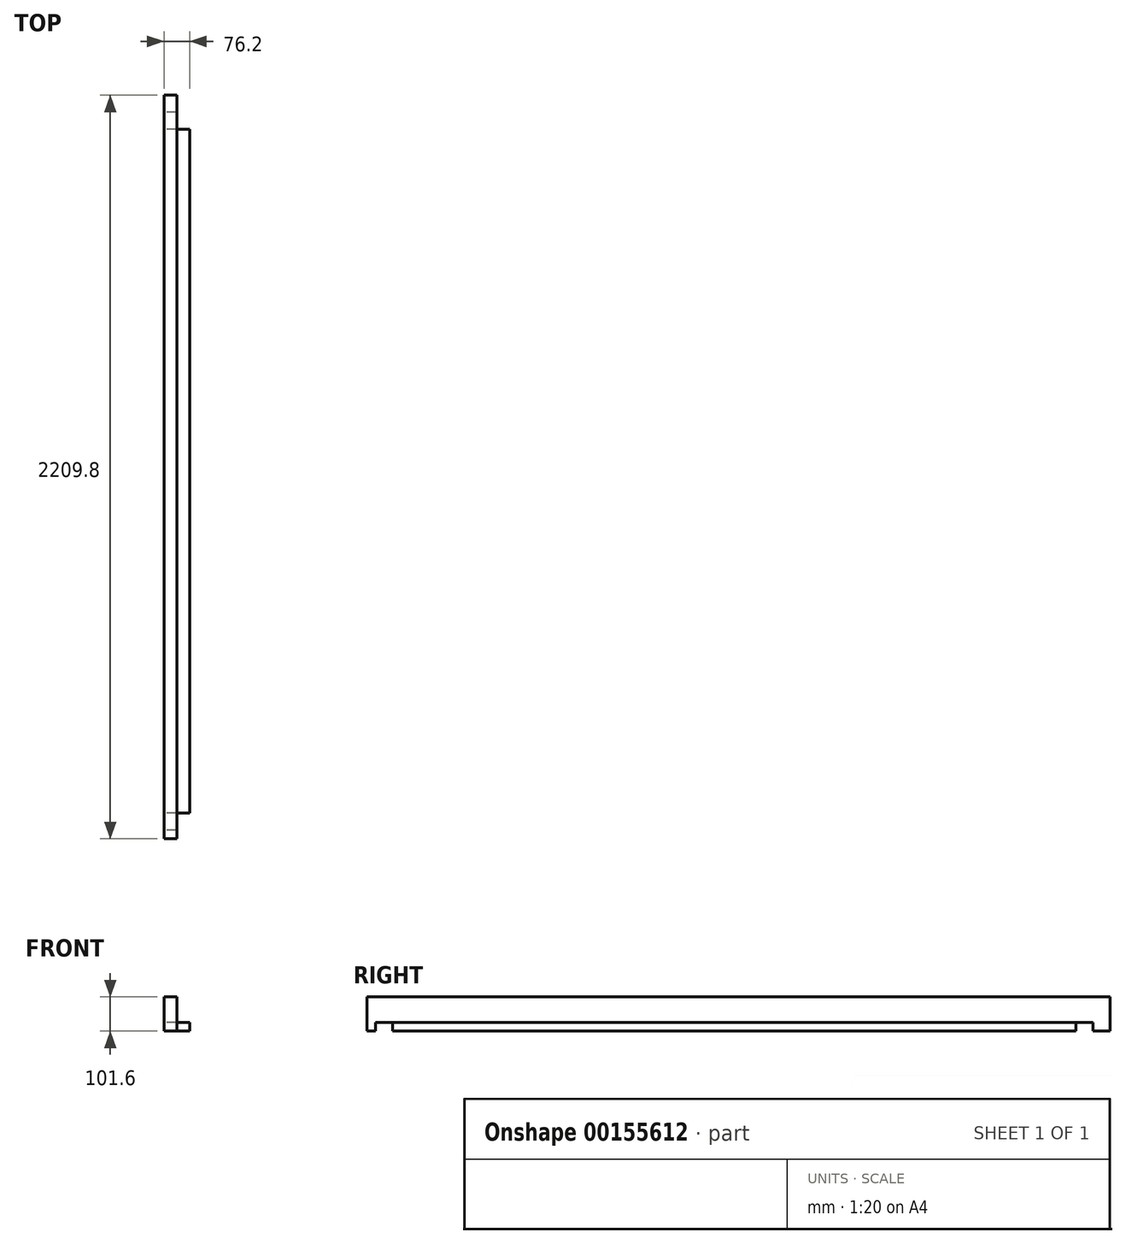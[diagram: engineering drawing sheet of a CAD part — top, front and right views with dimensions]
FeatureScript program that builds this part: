
annotation { "Feature Type Name" : "Feature", "Feature Type Description" : "" }
export const myFeature = defineFeature(function(context is Context, id is Id, definition is map)
    precondition{}
    {
        {
            var Q0;
            Q0=qCreatedBy(makeId("Right.planeOp"),FACE);
            var sketch = newSketch(context, id + "F0", { "sketchPlane" : qUnion([Q0])});
            skLineSegment(sketch, "E0.bottom", {"start": v(-1104.9, 50.8) * mm, "end": v(1104.9, 50.8) * mm});
            skLineSegment(sketch, "E0.top", {"start": v(-1104.9, -50.8) * mm, "end": v(1104.9, -50.8) * mm});
            skLineSegment(sketch, "E0.left", {"start": v(-1104.9, 50.8) * mm, "end": v(-1104.9, -50.8) * mm});
            skLineSegment(sketch, "E0.right", {"start": v(1104.9, 50.8) * mm, "end": v(1104.9, -50.8) * mm});
            skPoint(sketch, "E0.middle", {"position": v(0, 0) * mm});
            skLineSegment(sketch, "E1.bottom", {"start": v(1054.1, -50.8) * mm, "end": v(1003.3, -50.8) * mm});
            skLineSegment(sketch, "E1.top", {"start": v(1054.1, -25.4) * mm, "end": v(1003.3, -25.4) * mm});
            skLineSegment(sketch, "E1.left", {"start": v(1054.1, -50.8) * mm, "end": v(1054.1, -25.4) * mm});
            skLineSegment(sketch, "E1.right", {"start": v(1003.3, -50.8) * mm, "end": v(1003.3, -25.4) * mm});
            skLineSegment(sketch, "E2.bottom", {"start": v(-1079.5, -50.8) * mm, "end": v(-1028.7, -50.8) * mm});
            skLineSegment(sketch, "E2.top", {"start": v(-1079.5, -25.4) * mm, "end": v(-1028.7, -25.4) * mm});
            skLineSegment(sketch, "E2.left", {"start": v(-1079.5, -50.8) * mm, "end": v(-1079.5, -25.4) * mm});
            skLineSegment(sketch, "E2.right", {"start": v(-1028.7, -50.8) * mm, "end": v(-1028.7, -25.4) * mm});
            skSolve(sketch);
        }
        {
            var Q0;
            Q0=makeQuery(id+"F0.imprint","IMPRINT",FACE,{"disambiguationData":[TD([[makeQuery(id+"F0.imprint","IMPRINT",EDGE,{"derivedFrom":sQuery(id+"F0.wireOp",EDGE,"E0.bottom")}),-1.0]])]});
            extrude(context, id + "F1", {"entities" : qUnion([Q0]), "depth" : 38.1 * mm});
        }
        {
            var Q0;
            Q0=makeQuery(id+"F1.opExtrude","SWEPT_FACE",FACE,{"disambiguationData":[OSD([sQuery(id+"F0.wireOp",EDGE,"E0.right")])]});
            var sketch = newSketch(context, id + "F2", { "sketchPlane" : qUnion([Q0])});
            skLineSegment(sketch, "E3.bottom", {"start": v(-38.1, -50.8) * mm, "end": v(-76.2, -50.8) * mm});
            skLineSegment(sketch, "E3.top", {"start": v(-38.1, -25.4) * mm, "end": v(-76.2, -25.4) * mm});
            skLineSegment(sketch, "E3.left", {"start": v(-38.1, -50.8) * mm, "end": v(-38.1, -25.4) * mm});
            skLineSegment(sketch, "E3.right", {"start": v(-76.2, -50.8) * mm, "end": v(-76.2, -25.4) * mm});
            skSolve(sketch);
        }
        {
            var Q0;
            Q0=makeQuery(id+"F2.imprint","IMPRINT",FACE,{"disambiguationData":[TD([[makeQuery(id+"F2.imprint","IMPRINT",EDGE,{"derivedFrom":sQuery(id+"F2.wireOp",EDGE,"E3.bottom")}),-1.0]])]});
            var Q1;
            Q1=makeQuery(id+"F1.opExtrude","SWEPT_FACE",FACE,{"disambiguationData":[OSD([sQuery(id+"F0.wireOp",EDGE,"E1.right")])]});
            extrude(context, id + "F3", {"entities" : qUnion([Q0]), "oppositeDirection" : true, "endBoundEntityFace" : qUnion([Q1]), "depth" : 2133.6 * mm});
        }
        {
            var Q0;
            Q0 = qSketchRegion(id + "F2", true);
            extrude(context, id + "F4", {"entities" : qUnion([Q0]), "operationType" : NewBodyOperationType.REMOVE, "oppositeDirection" : true, "depth" : 101.6 * mm});
        }
    });
